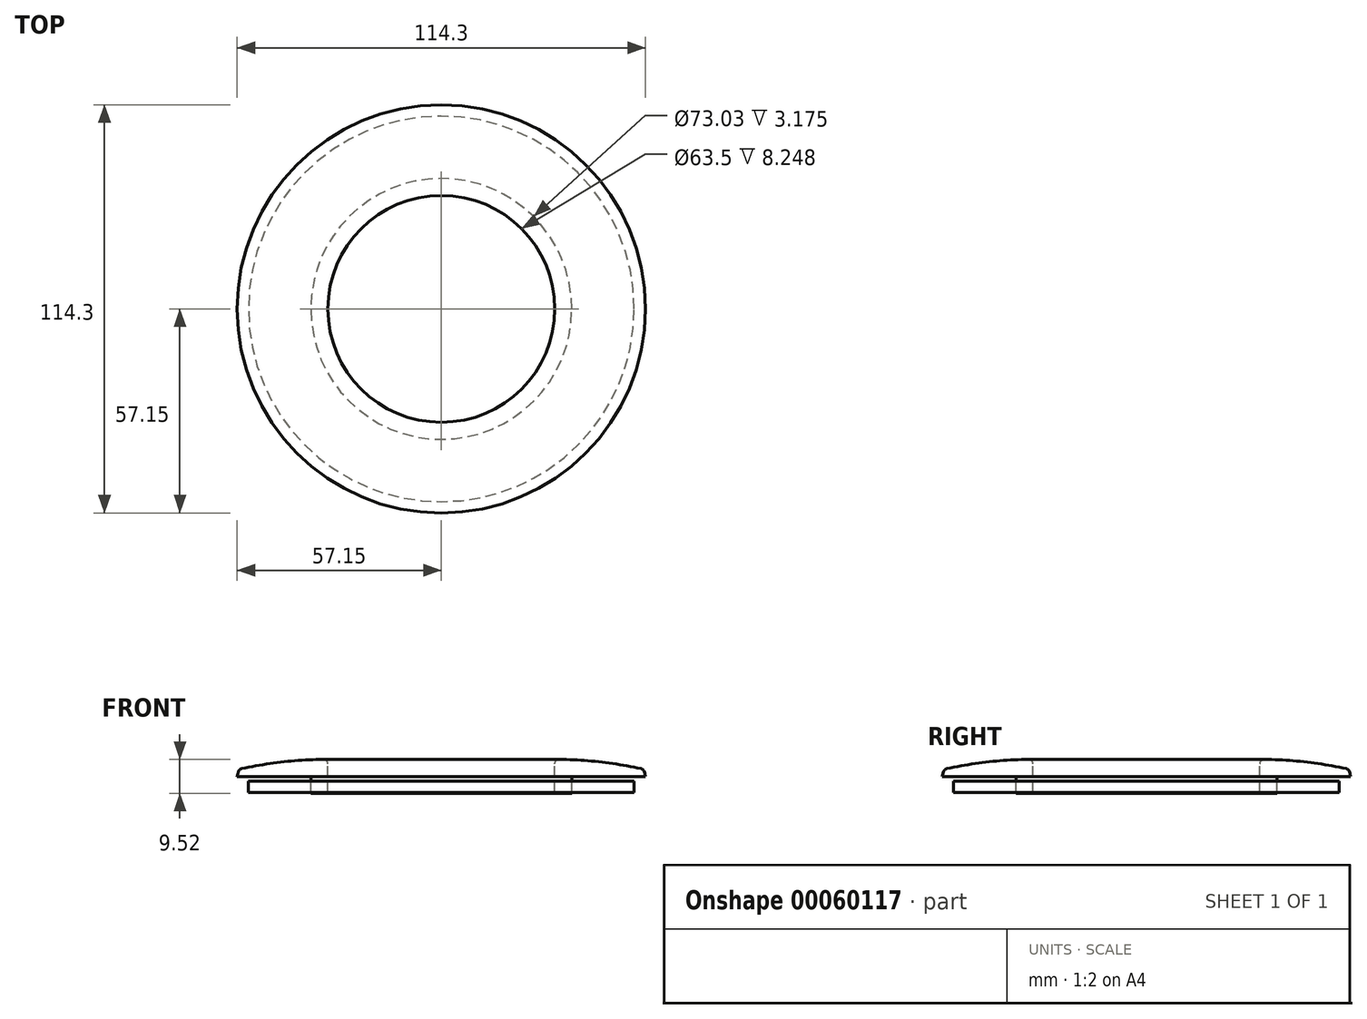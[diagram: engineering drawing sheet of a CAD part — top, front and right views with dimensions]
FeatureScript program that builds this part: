
annotation { "Feature Type Name" : "Feature", "Feature Type Description" : "" }
export const myFeature = defineFeature(function(context is Context, id is Id, definition is map)
    precondition{}
    {
        {
            var Q0;
            Q0=qCreatedBy(makeId("Front.planeOp"),FACE);
            var sketch = newSketch(context, id + "F0", { "sketchPlane" : qUnion([Q0])});
            skLineSegment(sketch, "E0", {"start": v(0, 30.42) * mm, "end": v(0, -33.3) * mm, "construction": true});
            skLineSegment(sketch, "E1", {"start": v(-31.75, 4.76) * mm, "end": v(-31.75, -4.76) * mm});
            skLineSegment(sketch, "E2", {"start": v(-31.75, -4.76) * mm, "end": v(-36.51, -4.76) * mm});
            skLineSegment(sketch, "E3", {"start": v(-36.51, 0) * mm, "end": v(-57.15, 0) * mm});
            skLineSegment(sketch, "E4", {"start": v(-34.77, 4.76) * mm, "end": v(-31.75, 4.76) * mm, "construction": true});
            skArc(sketch, "E5", {"start": v(-31.75, 4.76) * mm, "mid": v(-44.25, 4.08) * mm, "end": v(-56.6, 2.03) * mm});
            skLineSegment(sketch, "E6", {"start": v(-57.15, 0) * mm, "end": v(-56.6, 2.03) * mm});
            skLineSegment(sketch, "E7", {"start": v(0, 0) * mm, "end": v(-33.12, 0) * mm, "construction": true});
            skLineSegment(sketch, "E8.bottom", {"start": v(-53.97, -1.27) * mm, "end": v(-36.51, -1.27) * mm});
            skLineSegment(sketch, "E8.top", {"start": v(-53.98, -4.45) * mm, "end": v(-36.51, -4.44) * mm});
            skLineSegment(sketch, "E8.left", {"start": v(-53.97, -1.27) * mm, "end": v(-53.97, -4.45) * mm});
            skLineSegment(sketch, "E9", {"start": v(-36.51, 0) * mm, "end": v(-36.51, -4.76) * mm});
            skSolve(sketch);
        }
        {
            var Q0;
            Q0=makeQuery(id+"F0.imprint","IMPRINT",FACE,{"disambiguationData":[TD([[makeQuery(id+"F0.imprint","IMPRINT",EDGE,{"derivedFrom":sQuery(id+"F0.wireOp",EDGE,"E1")}),-1.0]])]});
            var Q1;
            Q1=sQuery(id+"F0.wireOp",EDGE,"E0");
            revolve(context, id + "F1", {"entities" : qUnion([Q0]), "axis" : qUnion([Q1]), "revolveType" : RevolveType.FULL});
        }
        {
            var Q0;
            Q0=makeQuery(id+"F1.opRevolve","SWEPT_EDGE",EDGE,{"disambiguationData":[OSD([sQuery(id+"F0.wireOp",EDGE,"E5"),sQuery(id+"F0.wireOp",EDGE,"E6")])]});
            var Q1;
            Q1=makeQuery(id+"F1.opRevolve","SWEPT_EDGE",EDGE,{"disambiguationData":[OSD([sQuery(id+"F0.wireOp",EDGE,"E1"),sQuery(id+"F0.wireOp",EDGE,"E5")])]});
            fillet(context, id + "F2", {"entities" : qUnion([Q0, Q1]), "radius" : 1.27 * mm, "tangentPropagation" : true, "allowEdgeOverflow" : false});
        }
        {
            var Q0;
            {var subQ5=sQuery(id+"F0.wireOp",EDGE,"E8.bottom");Q0=makeQuery(id+"F0.imprint","IMPRINT",FACE,{"disambiguationData":[TD([[makeQuery(id+"F0.imprint","IMPRINT",EDGE,{"derivedFrom":subQ5}),-1.0]])]});}
            var Q1;
            Q1=sQuery(id+"F0.wireOp",EDGE,"E0");
            revolve(context, id + "F3", {"entities" : qUnion([Q0]), "axis" : qUnion([Q1]), "revolveType" : RevolveType.FULL});
        }
    });
